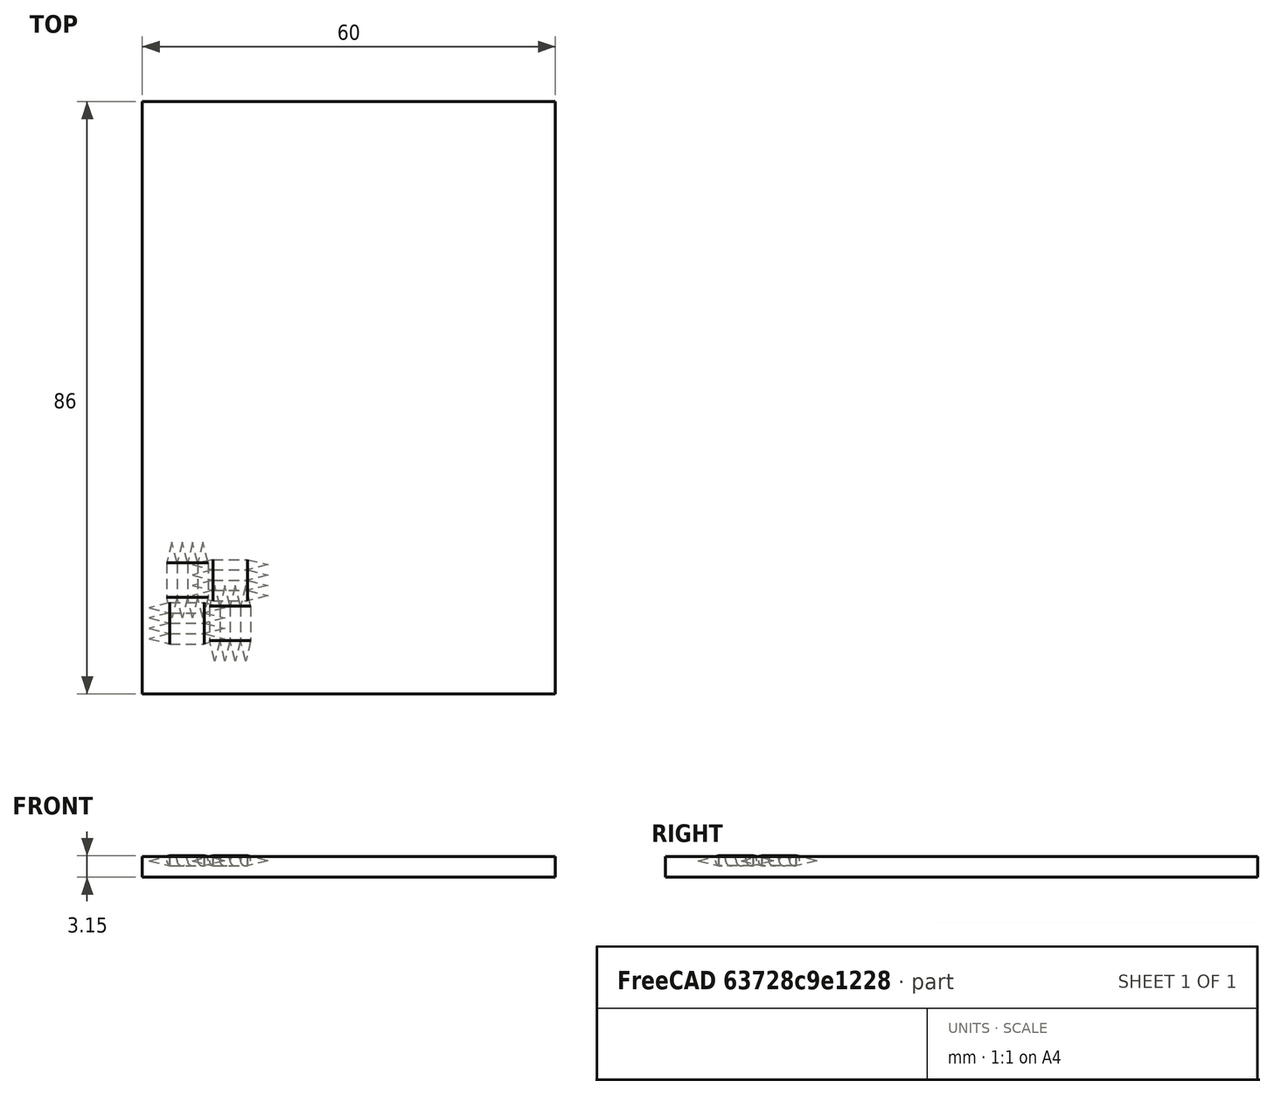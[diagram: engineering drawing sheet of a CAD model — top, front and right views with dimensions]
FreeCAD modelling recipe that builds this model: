
FCSTD DOCUMENT  (FreeCAD 0.14R3251)
Label: front-frame-plate
License: CC-BY 3.0
LicenseURL: http://creativecommons.org/licenses/by/3.0/
objects: Part::MultiFuse×20, Part::Cone×5, Part::Cylinder×4, Part::Mirroring×4, Part::Box×1
note: 34 computed .brp shape members not serialized (recipe doc carries the construction recipe); baked Part::Feature solids carry a one-line shape summary decoded from their .brp

FEATURE [Part::Cone] Cone
  Angle = 360
  Height = 3
  Placement = pos=(0,0,4) rot=(0,0,1;0rad)
  Radius1 = 0.75
  Radius2 = 0
FEATURE [Part::Cylinder] Cylinder
  Angle = 360
  Height = 5
  Radius = 0.75
FEATURE [Part::Mirroring] Part__Mirroring  label="Cone (Mirror #1)"
  Base = (0,0,0)
  Normal = (0,0,1)
  Placement = pos=(0,0,4) rot=(0,0,1;0rad)
  Source = -> Cone
FEATURE [Part::Cone] Cone001
  Angle = 360
  Height = 3
  Placement = pos=(0,0,5) rot=(0,0,1;0rad)
  Radius1 = 0.75
  Radius2 = 0
FEATURE [Part::MultiFuse] Fusion
  Placement = pos=(9,16,2.4) rot=(1,0,0;1.5708rad)
  Shapes = -> [Cylinder,Part__Mirroring,Cone001]
FEATURE [Part::Box] Box
  Height = 3
  Length = 60
  Width = 86
FEATURE [Part::Cone] Cone002
  Angle = 360
  Height = 3
  Placement = pos=(0,0,5) rot=(0,0,1;0rad)
  Radius1 = 0.75
  Radius2 = 0
FEATURE [Part::Mirroring] Part__Mirroring001  label="Cone (Mirror #1)001"
  Base = (0,0,0)
  Normal = (0,0,1)
  Placement = pos=(0,0,4) rot=(0,0,1;0rad)
  Source = -> Cone
FEATURE [Part::Cylinder] Cylinder001
  Angle = 360
  Height = 5
  Radius = 0.75
FEATURE [Part::MultiFuse] Fusion001
  Placement = pos=(10.5,16,2.4) rot=(1,0,0;1.5708rad)
  Shapes = -> [Cylinder001,Part__Mirroring001,Cone002]
FEATURE [Part::Cone] Cone003
  Angle = 360
  Height = 3
  Placement = pos=(0,0,5) rot=(0,0,1;0rad)
  Radius1 = 0.75
  Radius2 = 0
FEATURE [Part::Mirroring] Part__Mirroring002  label="Cone (Mirror #1)002"
  Base = (0,0,0)
  Normal = (0,0,1)
  Placement = pos=(0,0,4) rot=(0,0,1;0rad)
  Source = -> Cone
FEATURE [Part::Cylinder] Cylinder002
  Angle = 360
  Height = 5
  Radius = 0.75
FEATURE [Part::MultiFuse] Fusion002
  Placement = pos=(12,16,2.4) rot=(1,0,0;1.5708rad)
  Shapes = -> [Cylinder002,Part__Mirroring002,Cone003]
FEATURE [Part::Cone] Cone004
  Angle = 360
  Height = 3
  Placement = pos=(0,0,5) rot=(0,0,1;0rad)
  Radius1 = 0.75
  Radius2 = 0
FEATURE [Part::Mirroring] Part__Mirroring003  label="Cone (Mirror #1)003"
  Base = (0,0,0)
  Normal = (0,0,1)
  Placement = pos=(0,0,4) rot=(0,0,1;0rad)
  Source = -> Cone
FEATURE [Part::Cylinder] Cylinder003
  Angle = 360
  Height = 5
  Radius = 0.75
FEATURE [Part::MultiFuse] Fusion003
  Placement = pos=(13.5,16,2.4) rot=(1,0,0;1.5708rad)
  Shapes = -> [Cylinder003,Part__Mirroring003,Cone004]
FEATURE [Part::MultiFuse] Fusion004
  Placement = pos=(1.5,-3.25,0) rot=(0,0,1;0rad)
  Shapes = -> [Fusion,Fusion001,Fusion002,Fusion003]
FEATURE [Part::MultiFuse] Fusion006
  Placement = pos=(13.5,16,2.4) rot=(1,0,0;1.5708rad)
  Shapes = -> [Cylinder003,Part__Mirroring003,Cone004]
FEATURE [Part::MultiFuse] Fusion007
  Placement = pos=(10.5,16,2.4) rot=(1,0,0;1.5708rad)
  Shapes = -> [Cylinder001,Part__Mirroring001,Cone002]
FEATURE [Part::MultiFuse] Fusion008
  Placement = pos=(12,16,2.4) rot=(1,0,0;1.5708rad)
  Shapes = -> [Cylinder002,Part__Mirroring002,Cone003]
FEATURE [Part::MultiFuse] Fusion009
  Placement = pos=(9,16,2.4) rot=(1,0,0;1.5708rad)
  Shapes = -> [Cylinder,Part__Mirroring,Cone001]
FEATURE [Part::MultiFuse] Fusion005
  Placement = pos=(-4.7,3,0) rot=(0,0,1;0rad)
  Shapes = -> [Fusion009,Fusion007,Fusion008,Fusion006]
FEATURE [Part::MultiFuse] Fusion011
  Placement = pos=(13.5,16,2.4) rot=(1,0,0;1.5708rad)
  Shapes = -> [Cylinder003,Part__Mirroring003,Cone004]
FEATURE [Part::MultiFuse] Fusion012
  Placement = pos=(10.5,16,2.4) rot=(1,0,0;1.5708rad)
  Shapes = -> [Cylinder001,Part__Mirroring001,Cone002]
FEATURE [Part::MultiFuse] Fusion013
  Placement = pos=(12,16,2.4) rot=(1,0,0;1.5708rad)
  Shapes = -> [Cylinder002,Part__Mirroring002,Cone003]
FEATURE [Part::MultiFuse] Fusion014
  Placement = pos=(9,16,2.4) rot=(1,0,0;1.5708rad)
  Shapes = -> [Cylinder,Part__Mirroring,Cone001]
FEATURE [Part::MultiFuse] Fusion010
  Placement = pos=(20,-1,0) rot=(0,0,1;1.5708rad)
  Shapes = -> [Fusion014,Fusion012,Fusion013,Fusion011]
FEATURE [Part::MultiFuse] Fusion016
  Placement = pos=(13.5,16,2.4) rot=(1,0,0;1.5708rad)
  Shapes = -> [Cylinder003,Part__Mirroring003,Cone004]
FEATURE [Part::MultiFuse] Fusion017
  Placement = pos=(12,16,2.4) rot=(1,0,0;1.5708rad)
  Shapes = -> [Cylinder002,Part__Mirroring002,Cone003]
FEATURE [Part::MultiFuse] Fusion018
  Placement = pos=(10.5,16,2.4) rot=(1,0,0;1.5708rad)
  Shapes = -> [Cylinder001,Part__Mirroring001,Cone002]
FEATURE [Part::MultiFuse] Fusion019
  Placement = pos=(9,16,2.4) rot=(1,0,0;1.5708rad)
  Shapes = -> [Cylinder,Part__Mirroring,Cone001]
FEATURE [Part::MultiFuse] Fusion015
  Placement = pos=(26.25,5.25,0) rot=(0,0,1;1.5708rad)
  Shapes = -> [Fusion019,Fusion018,Fusion017,Fusion016]
